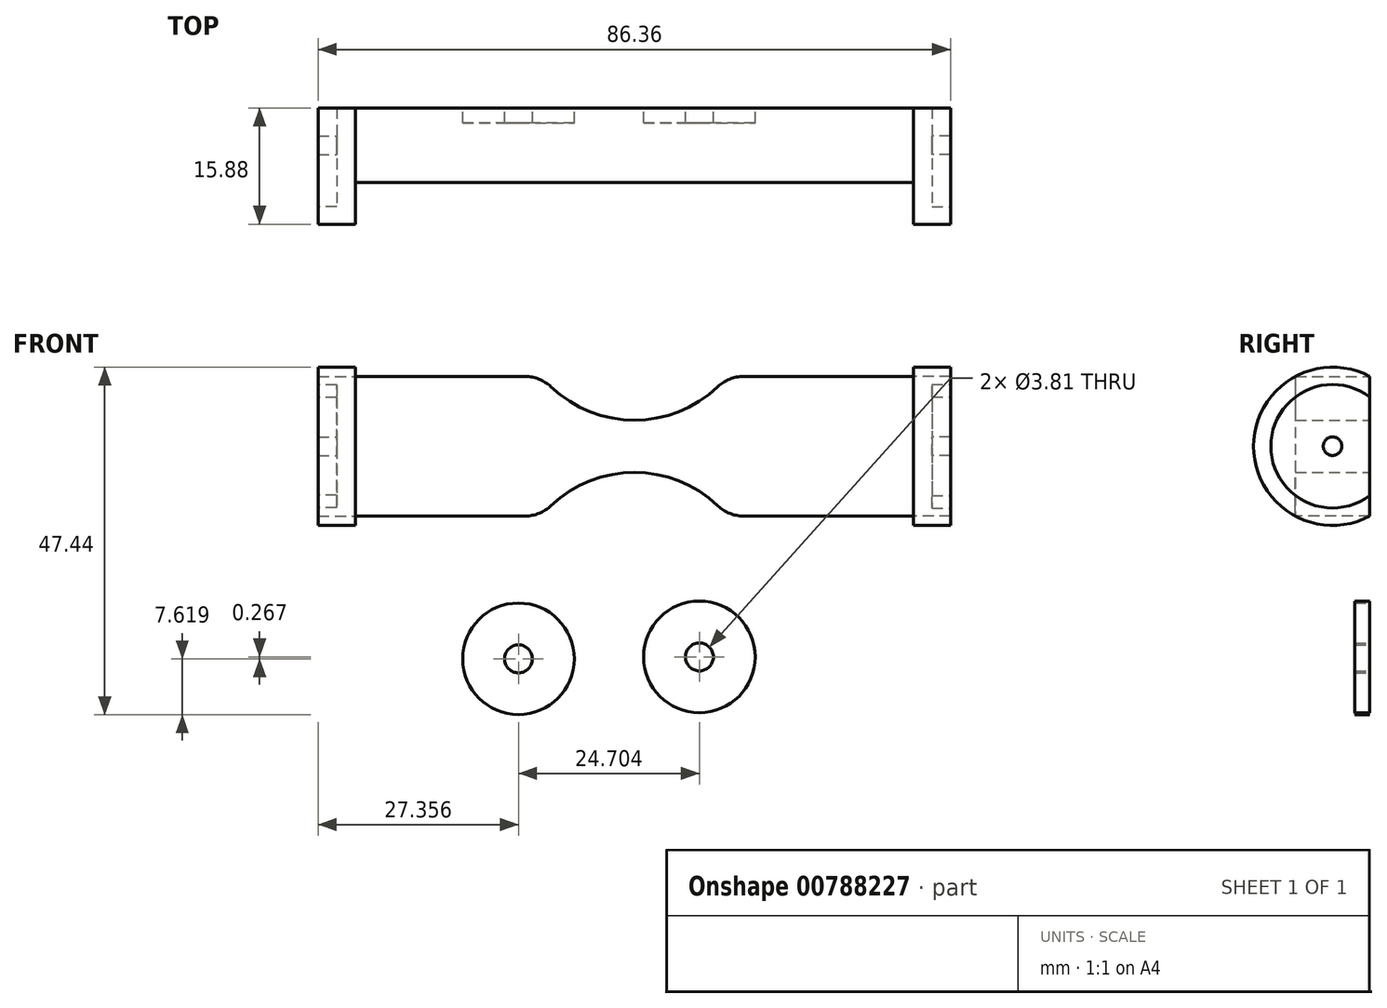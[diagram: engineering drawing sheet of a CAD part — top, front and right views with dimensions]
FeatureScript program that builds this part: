
annotation { "Feature Type Name" : "Feature", "Feature Type Description" : "" }
export const myFeature = defineFeature(function(context is Context, id is Id, definition is map)
    precondition{}
    {
        {
            var Q0;
            Q0=qCreatedBy(makeId("Front.planeOp"),FACE);
            var sketch = newSketch(context, id + "F0", { "sketchPlane" : qUnion([Q0])});
            skLineSegment(sketch, "E0.bottom", {"start": v(-46.98, 9.52) * mm, "end": v(-21.58, 9.53) * mm});
            skLineSegment(sketch, "E0.top", {"start": v(-46.98, -9.53) * mm, "end": v(-21.58, -9.52) * mm});
            skLineSegment(sketch, "E0.left", {"start": v(-46.98, 9.52) * mm, "end": v(-46.98, -9.53) * mm});
            skPoint(sketch, "E0.middle", {"position": v(-34.28, 0) * mm});
            skLineSegment(sketch, "E1.bottom", {"start": v(3.82, 9.52) * mm, "end": v(29.22, 9.52) * mm});
            skLineSegment(sketch, "E1.top", {"start": v(3.82, -9.53) * mm, "end": v(29.22, -9.53) * mm});
            skLineSegment(sketch, "E1.right", {"start": v(29.22, 9.52) * mm, "end": v(29.22, -9.53) * mm});
            skPoint(sketch, "E1.middle", {"position": v(16.52, 0) * mm});
            skArc(sketch, "E2", {"start": v(-21.58, 9.53) * mm, "mid": v(-8.88, 3.56) * mm, "end": v(3.82, 9.53) * mm});
            skArc(sketch, "E3", {"start": v(3.82, -9.53) * mm, "mid": v(-8.88, -3.56) * mm, "end": v(-21.58, -9.52) * mm});
            skSolve(sketch);
        }
        {
            var Q0;
            Q0=makeQuery(id+"F0.imprint","IMPRINT",FACE,{"disambiguationData":[TD([[makeQuery(id+"F0.imprint","IMPRINT",EDGE,{"derivedFrom":sQuery(id+"F0.wireOp",EDGE,"E0.bottom")}),-1.0]])]});
            extrude(context, id + "F1", {"entities" : qUnion([Q0]), "depth" : 10.16 * mm, "offsetDistance" : 25.4 * mm});
        }
        {
            var Q0;
            Q0=makeQuery(id+"F1.opExtrude","SWEPT_FACE",FACE,{"disambiguationData":[OSD([sQuery(id+"F0.wireOp",EDGE,"E1.right")])]});
            var sketch = newSketch(context, id + "F2", { "sketchPlane" : qUnion([Q0])});
            skCircle(sketch, "E4", {"center": v(-5.08, 0) * mm, "radius": 10.8 * mm});
            skSolve(sketch);
        }
        {
            var Q0;
            {var subQ1=sQuery(id+"F0.wireOp",EDGE,"E1.right");var subQ2=makeQuery(id+"F1.opExtrude","CAP_EDGE",EDGE,{"disambiguationData":[OSD([subQ1])],"isStart":false});Q0=makeQuery(id+"F2.imprint","IMPRINT",FACE,{"disambiguationData":[TD([[makeQuery(id+"F2.imprint","IMPRINT",EDGE,{"derivedFrom":subQ2}),-1.0]])]});}
            var Q1;
            {var subQ1=sQuery(id+"F0.wireOp",EDGE,"E1.right");var subQ2=makeQuery(id+"F1.opExtrude","SWEPT_EDGE",EDGE,{"disambiguationData":[OSD([sQuery(id+"F0.wireOp",EDGE,"E1.top"),subQ1])]});Q1=makeQuery(id+"F2.imprint","IMPRINT",FACE,{"disambiguationData":[TD([[makeQuery(id+"F2.imprint","IMPRINT",EDGE,{"derivedFrom":subQ2}),-1.0]])]});}
            var Q2;
            {var subQ1=sQuery(id+"F0.wireOp",EDGE,"E1.right");var subQ2=makeQuery(id+"F1.opExtrude","SWEPT_EDGE",EDGE,{"disambiguationData":[OSD([sQuery(id+"F0.wireOp",EDGE,"E1.bottom"),subQ1])]});Q2=makeQuery(id+"F2.imprint","IMPRINT",FACE,{"disambiguationData":[TD([[makeQuery(id+"F2.imprint","IMPRINT",EDGE,{"derivedFrom":subQ2}),1.0]])]});}
            var Q3;
            {var subQ0=sQuery(id+"F0.wireOp",EDGE,"E1.right");Q3=makeQuery(id+"F2.imprint","IMPRINT",FACE,{"disambiguationData":[TD([[makeQuery(id+"F2.imprint","IMPRINT",EDGE,{"derivedFrom":makeQuery(id+"F1.opExtrude","CAP_EDGE",EDGE,{"disambiguationData":[OSD([subQ0])],"isStart":true})}),-1.0]])]});}
            extrude(context, id + "F3", {"entities" : qUnion([Q0, Q1, Q2, Q3]), "operationType" : NewBodyOperationType.ADD, "depth" : 5.08 * mm, "offsetDistance" : 25.4 * mm});
        }
        {
            var Q0;
            Q0=makeQuery(id+"F3.opExtrude","CAP_FACE",FACE,{"disambiguationData":[OSD([sQuery(id+"F0.wireOp",EDGE,"E1.right"),sQuery(id+"F2.wireOp",EDGE,"E4")])],"isStart":false});
            var sketch = newSketch(context, id + "F4", { "sketchPlane" : qUnion([Q0])});
            skCircle(sketch, "E5", {"center": v(-5.08, 0) * mm, "radius": 8.42 * mm});
            skSolve(sketch);
        }
        {
            var Q0;
            {var subQ0=sQuery(id+"F4.wireOp",EDGE,"E5");var subQ1=makeQuery(id+"F3.opExtrude","CAP_EDGE",EDGE,{"disambiguationData":[OSD([sQuery(id+"F0.wireOp",EDGE,"E1.right")])],"isStart":false});var subQ2=makeQuery(id+"F4.imprint","INTERSECT",VERTEX,{"disambiguationData":[OD(0.0)],"derivedFrom":[subQ1,subQ0]});Q0=makeQuery(id+"F4.imprint","IMPRINT",FACE,{"disambiguationData":[TD([[makeQuery(id+"F4.imprint","IMPRINT",EDGE,{"disambiguationData":[TD([[subQ2,-1.0]])],"derivedFrom":subQ0}),1.0]])]});}
            extrude(context, id + "F5", {"entities" : qUnion([Q0]), "operationType" : NewBodyOperationType.REMOVE, "oppositeDirection" : true, "depth" : 2.54 * mm, "offsetDistance" : 25.4 * mm});
        }
        {
            var Q0;
            Q0=makeQuery(id+"F1.opExtrude","SWEPT_FACE",FACE,{"disambiguationData":[OSD([sQuery(id+"F0.wireOp",EDGE,"E0.left")])]});
            var sketch = newSketch(context, id + "F6", { "sketchPlane" : qUnion([Q0])});
            skArc(sketch, "E6", {"start": v(0, -9.53) * mm, "mid": v(15.88, 0) * mm, "end": v(0, 9.53) * mm});
            skSolve(sketch);
        }
        {
            var Q0;
            Q0=makeQuery(id+"F6.imprint","IMPRINT",FACE,{"disambiguationData":[TD([[makeQuery(id+"F6.imprint","IMPRINT",EDGE,{"derivedFrom":sQuery(id+"F6.wireOp",EDGE,"E6")}),1.0]])]});
            var Q1;
            {var subQ0=sQuery(id+"F0.wireOp",EDGE,"E0.left");Q1=makeQuery(id+"F6.imprint","IMPRINT",FACE,{"disambiguationData":[TD([[makeQuery(id+"F6.imprint","IMPRINT",EDGE,{"derivedFrom":makeQuery(id+"F1.opExtrude","CAP_EDGE",EDGE,{"disambiguationData":[OSD([subQ0])],"isStart":true})}),1.0]])]});}
            extrude(context, id + "F7", {"entities" : qUnion([Q0, Q1]), "operationType" : NewBodyOperationType.ADD, "depth" : 5.08 * mm, "offsetDistance" : 25.4 * mm});
        }
        {
            var Q0;
            Q0=makeQuery(id+"F7.opExtrude","CAP_FACE",FACE,{"disambiguationData":[OSD([sQuery(id+"F0.wireOp",EDGE,"E0.left"),sQuery(id+"F6.wireOp",EDGE,"E6")])],"isStart":false});
            var sketch = newSketch(context, id + "F8", { "sketchPlane" : qUnion([Q0])});
            skCircle(sketch, "E7", {"center": v(5.08, 0) * mm, "radius": 8.38 * mm});
            skSolve(sketch);
        }
        {
            var Q0;
            {var subQ0=sQuery(id+"F8.wireOp",EDGE,"E7");var subQ1=makeQuery(id+"F7.opExtrude","CAP_EDGE",EDGE,{"disambiguationData":[OSD([sQuery(id+"F0.wireOp",EDGE,"E0.left")])],"isStart":false});var subQ2=makeQuery(id+"F8.imprint","INTERSECT",VERTEX,{"disambiguationData":[OD(0.0)],"derivedFrom":[subQ1,subQ0]});Q0=makeQuery(id+"F8.imprint","IMPRINT",FACE,{"disambiguationData":[TD([[makeQuery(id+"F8.imprint","IMPRINT",EDGE,{"disambiguationData":[TD([[subQ2,1.0]])],"derivedFrom":subQ0}),1.0]])]});}
            extrude(context, id + "F9", {"entities" : qUnion([Q0]), "operationType" : NewBodyOperationType.REMOVE, "oppositeDirection" : true, "depth" : 2.54 * mm, "offsetDistance" : 25.4 * mm});
        }
        {
            var Q0;
            Q0=makeQuery(id+"F5.boolean.opBoolean","COPY",FACE,{"derivedFrom":makeQuery(id+"F5.opExtrude","CAP_FACE",FACE,{"disambiguationData":[OSD([sQuery(id+"F0.wireOp",EDGE,"E1.right"),sQuery(id+"F4.wireOp",EDGE,"E5")])],"isStart":false})});
            var sketch = newSketch(context, id + "F10", { "sketchPlane" : qUnion([Q0])});
            skPoint(sketch, "E8", {"position": v(-5.08, 0) * mm});
            skCircle(sketch, "E9", {"center": v(-5.08, 0) * mm, "radius": 1.27 * mm});
            skSolve(sketch);
        }
        {
            var Q0;
            Q0=makeQuery(id+"F10.imprint","IMPRINT",FACE,{"disambiguationData":[TD([[makeQuery(id+"F10.imprint","IMPRINT",EDGE,{"derivedFrom":sQuery(id+"F10.wireOp",EDGE,"E9")}),1.0]])]});
            extrude(context, id + "F11", {"entities" : qUnion([Q0]), "operationType" : NewBodyOperationType.ADD, "depth" : 2.54 * mm, "offsetDistance" : 25.4 * mm});
        }
        {
            var Q0;
            Q0=makeQuery(id+"F9.boolean.opBoolean","COPY",FACE,{"derivedFrom":makeQuery(id+"F9.opExtrude","CAP_FACE",FACE,{"disambiguationData":[OSD([sQuery(id+"F0.wireOp",EDGE,"E0.left"),sQuery(id+"F8.wireOp",EDGE,"E7")])],"isStart":false})});
            var sketch = newSketch(context, id + "F12", { "sketchPlane" : qUnion([Q0])});
            skPoint(sketch, "E10", {"position": v(5.08, 0) * mm});
            skCircle(sketch, "E11", {"center": v(5.08, 0) * mm, "radius": 1.27 * mm});
            skSolve(sketch);
        }
        {
            var Q0;
            Q0=makeQuery(id+"F12.imprint","IMPRINT",FACE,{"disambiguationData":[TD([[makeQuery(id+"F12.imprint","IMPRINT",EDGE,{"derivedFrom":sQuery(id+"F12.wireOp",EDGE,"E11")}),1.0]])]});
            extrude(context, id + "F13", {"entities" : qUnion([Q0]), "operationType" : NewBodyOperationType.ADD, "depth" : 2.54 * mm, "offsetDistance" : 25.4 * mm});
        }
        {
            var Q0;
            Q0=qCreatedBy(makeId("Front.planeOp"),FACE);
            var sketch = newSketch(context, id + "F14", { "sketchPlane" : qUnion([Q0])});
            skCircle(sketch, "E12", {"center": v(0, -28.75) * mm, "radius": 7.62 * mm});
            skCircle(sketch, "E13", {"center": v(-24.7, -29.02) * mm, "radius": 7.62 * mm});
            skCircle(sketch, "E14", {"center": v(0, -28.75) * mm, "radius": 1.9 * mm});
            skCircle(sketch, "E15", {"center": v(-24.7, -29.02) * mm, "radius": 1.9 * mm});
            skSolve(sketch);
        }
        {
            var Q0;
            Q0=makeQuery(id+"F14.imprint","IMPRINT",FACE,{"disambiguationData":[TD([[makeQuery(id+"F14.imprint","IMPRINT",EDGE,{"derivedFrom":sQuery(id+"F14.wireOp",EDGE,"E12")}),1.0]])]});
            var Q1;
            Q1=makeQuery(id+"F14.imprint","IMPRINT",FACE,{"disambiguationData":[TD([[makeQuery(id+"F14.imprint","IMPRINT",EDGE,{"derivedFrom":sQuery(id+"F14.wireOp",EDGE,"E13")}),1.0]])]});
            extrude(context, id + "F15", {"entities" : qUnion([Q0, Q1]), "depth" : 2.03 * mm, "offsetDistance" : 25.4 * mm});
        }
        {
            var Q0;
            Q0=makeQuery(id+"F1.opExtrude","SWEPT_EDGE",EDGE,{"disambiguationData":[OSD([sQuery(id+"F0.wireOp",EDGE,"E0.bottom"),sQuery(id+"F0.wireOp",EDGE,"E2")])]});
            var Q1;
            Q1=makeQuery(id+"F1.opExtrude","SWEPT_EDGE",EDGE,{"disambiguationData":[OSD([sQuery(id+"F0.wireOp",EDGE,"E1.bottom"),sQuery(id+"F0.wireOp",EDGE,"E2")])]});
            var Q2;
            Q2=makeQuery(id+"F1.opExtrude","SWEPT_EDGE",EDGE,{"disambiguationData":[OSD([sQuery(id+"F0.wireOp",EDGE,"E1.top"),sQuery(id+"F0.wireOp",EDGE,"E3")])]});
            var Q3;
            Q3=makeQuery(id+"F1.opExtrude","SWEPT_EDGE",EDGE,{"disambiguationData":[OSD([sQuery(id+"F0.wireOp",EDGE,"E0.top"),sQuery(id+"F0.wireOp",EDGE,"E3")])]});
            fillet(context, id + "F16", {"entities" : qUnion([Q0, Q1, Q2, Q3]), "radius" : 5.08 * mm, "tangentPropagation" : true, "allowEdgeOverflow" : false});
        }
    });
